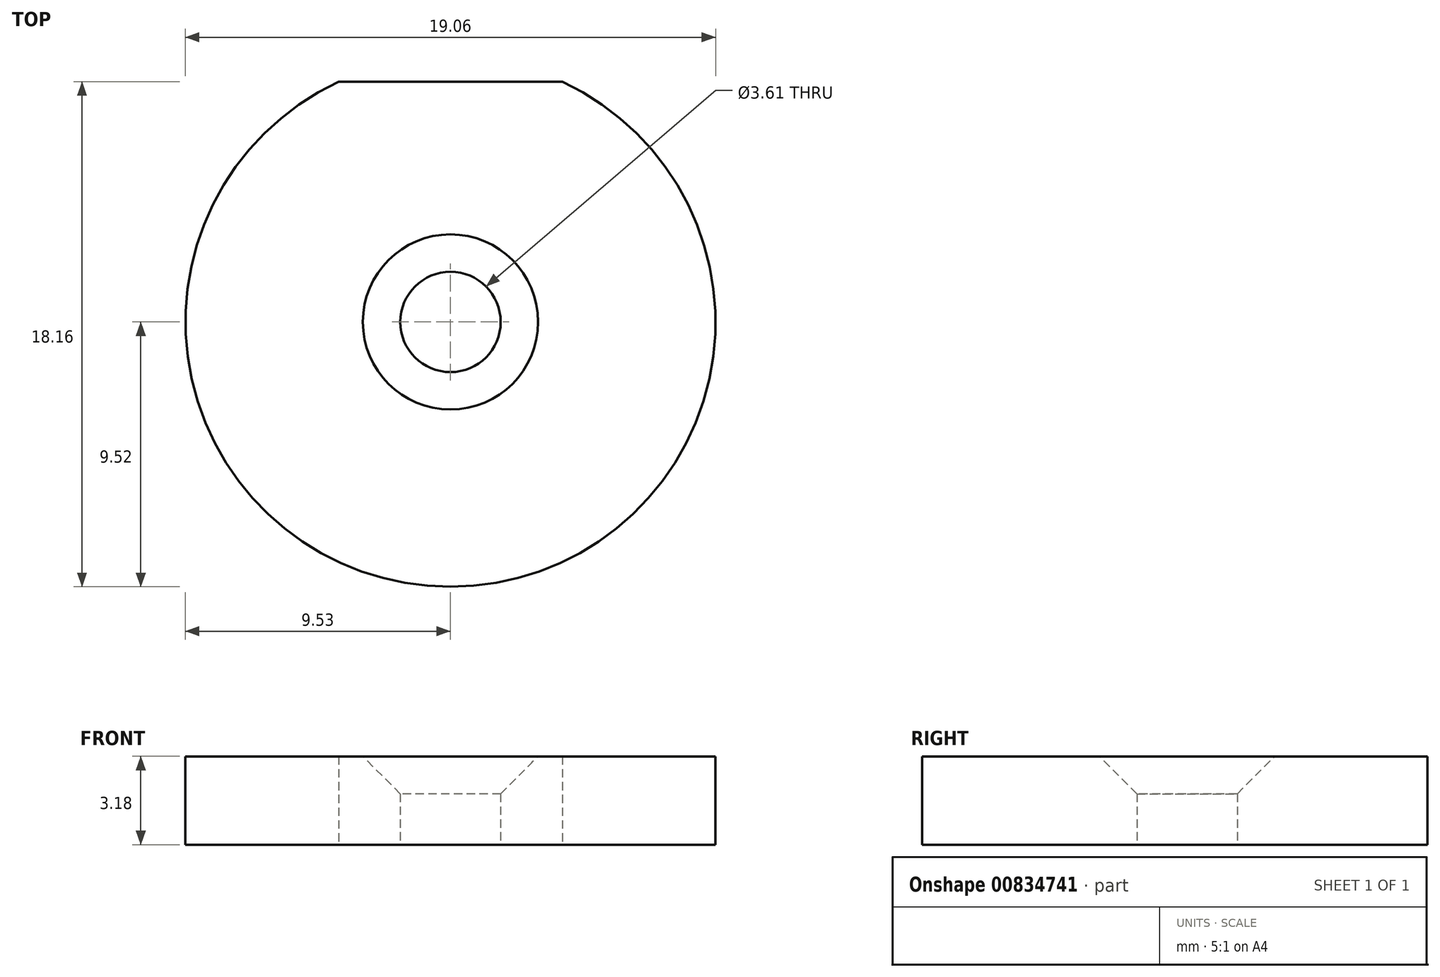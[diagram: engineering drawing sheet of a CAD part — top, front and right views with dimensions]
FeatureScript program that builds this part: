
annotation { "Feature Type Name" : "Feature", "Feature Type Description" : "" }
export const myFeature = defineFeature(function(context is Context, id is Id, definition is map)
    precondition{}
    {
        {
            var Q0;
            Q0=qCreatedBy(makeId("Top.planeOp"),FACE);
            var sketch = newSketch(context, id + "F0", { "sketchPlane" : qUnion([Q0])});
            skArc(sketch, "E0", {"start": v(-4.02, 8.64) * mm, "mid": v(0, -9.53) * mm, "end": v(4.02, 8.64) * mm});
            skLineSegment(sketch, "E1", {"start": v(-4.02, 8.64) * mm, "end": v(4.02, 8.64) * mm});
            skCircle(sketch, "E2", {"center": v(0, 0) * mm, "radius": 1.8 * mm});
            skCircle(sketch, "E3", {"center": v(0, 0) * mm, "radius": 3.15 * mm});
            skSolve(sketch);
        }
        {
            var Q0;
            Q0=makeQuery(id+"F0.imprint","IMPRINT",FACE,{"disambiguationData":[TD([[makeQuery(id+"F0.imprint","IMPRINT",EDGE,{"derivedFrom":sQuery(id+"F0.wireOp",EDGE,"E0")}),1.0]])]});
            var Q1;
            Q1=makeQuery(id+"F0.imprint","IMPRINT",FACE,{"disambiguationData":[TD([[makeQuery(id+"F0.imprint","IMPRINT",EDGE,{"derivedFrom":sQuery(id+"F0.wireOp",EDGE,"E0")}),-1.0]])]});
            var Q2;
            Q2=makeQuery(id+"F0.imprint","IMPRINT",FACE,{"disambiguationData":[TD([[makeQuery(id+"F0.imprint","IMPRINT",EDGE,{"derivedFrom":sQuery(id+"F0.wireOp",EDGE,"E2")}),-1.0]])]});
            extrude(context, id + "F1", {"entities" : qUnion([Q0, Q1, Q2]), "depth" : 3.17 * mm, "offsetDistance" : 25 * mm});
        }
        {
            var Q0;
            Q0=makeQuery(id+"F1.opExtrude","CAP_EDGE",EDGE,{"disambiguationData":[OSD([sQuery(id+"F0.wireOp",EDGE,"E2")])],"isStart":false});
            chamfer(context, id + "F2", {"entities" : qUnion([Q0]), "chamferType" : ChamferType.OFFSET_ANGLE, "width" : 1.35 * mm, "oppositeDirection" : false, "angle" : 45 * degree, "tangentPropagation" : true});
        }
    });
